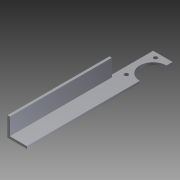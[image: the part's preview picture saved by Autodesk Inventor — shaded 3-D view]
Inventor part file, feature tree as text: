
AUTODESK INVENTOR PART (.ipt)
format: ipt  version: 2012 (Build 160160000, 160)  size: 86,528 bytes
history: native  units: in
note: dims shown in document units (in); Inventor stores cm internally (conversion verified against a paired STEP export)
features: other x3, sketch x2
ambient origin geometry x8: Origin, YZ Plane, XZ Plane, XY Plane, X Axis, Y Axis, Z Axis, Center Point
bodies: Solid1 (feature_tree)
feature tree (5):
  other  "8 ball corner L.ipt"
  other  "Solid1::8 ball corner L.ipt"
  sketch  "Sketch1"  dims[d0=0.3937in]
  sketch  "Sketch2"
  other  "TaggingFeature1"
